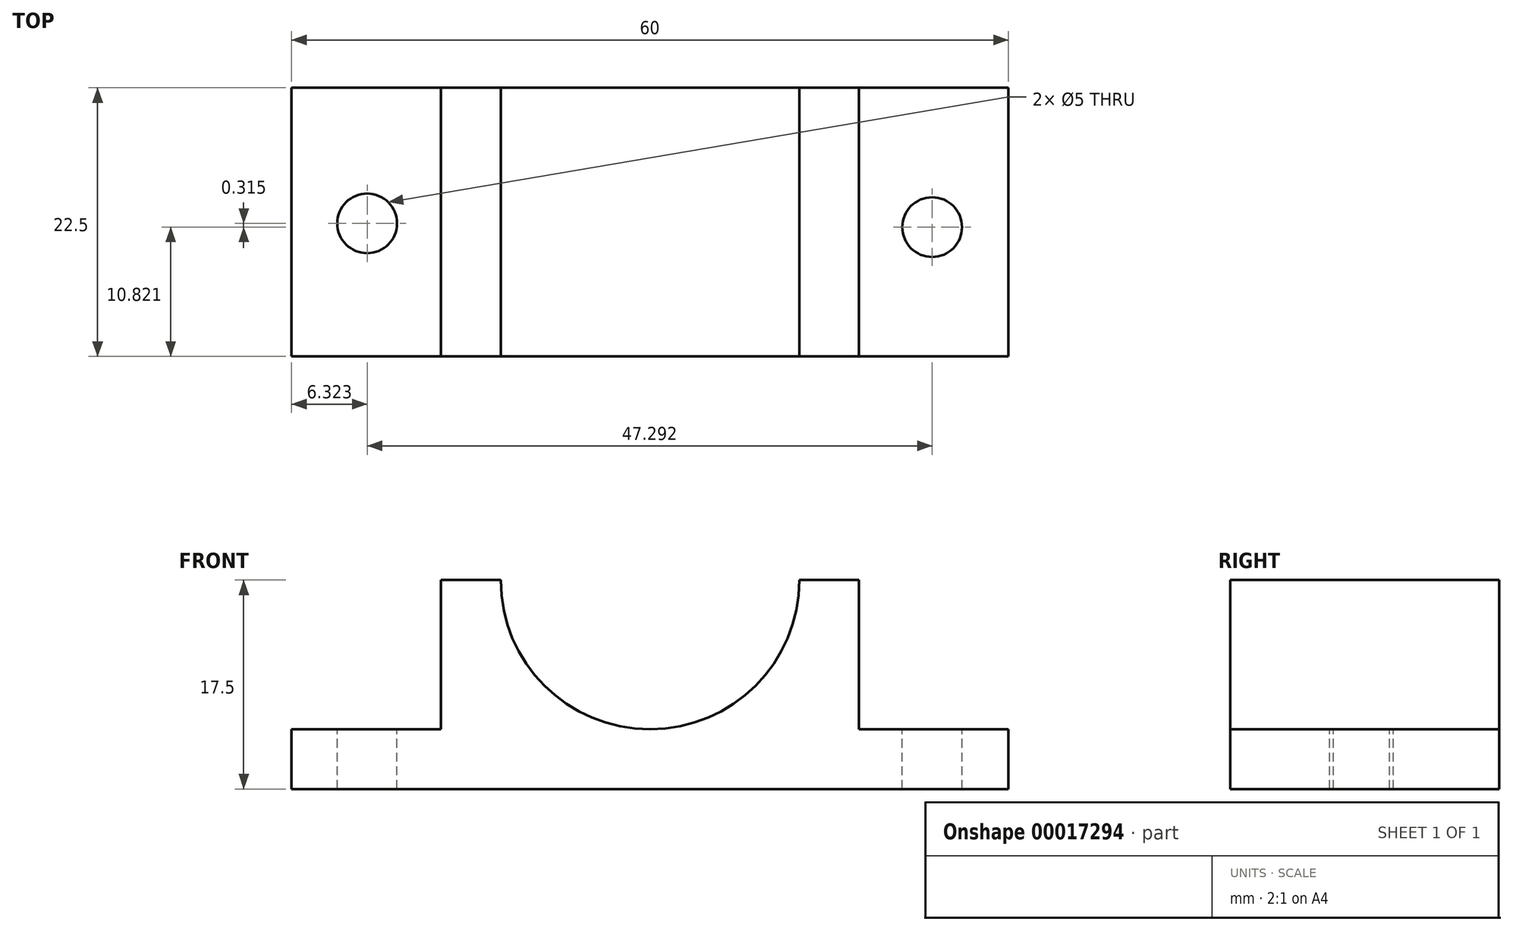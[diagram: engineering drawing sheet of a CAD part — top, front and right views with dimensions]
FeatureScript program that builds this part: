
annotation { "Feature Type Name" : "Feature", "Feature Type Description" : "" }
export const myFeature = defineFeature(function(context is Context, id is Id, definition is map)
    precondition{}
    {
        {
            var Q0;
            Q0=qCreatedBy(makeId("Front.planeOp"),FACE);
            var sketch = newSketch(context, id + "F0", { "sketchPlane" : qUnion([Q0])});
            skLineSegment(sketch, "E0", {"start": v(0, 0) * mm, "end": v(0, 5) * mm});
            skLineSegment(sketch, "E1", {"start": v(0, 5) * mm, "end": v(-12.5, 5) * mm});
            skLineSegment(sketch, "E2", {"start": v(-12.5, 5) * mm, "end": v(-12.5, 17.5) * mm});
            skLineSegment(sketch, "E3", {"start": v(-12.5, 17.5) * mm, "end": v(-17.5, 17.5) * mm});
            skLineSegment(sketch, "E4", {"start": v(-17.5, 17.5) * mm, "end": v(-42.5, 17.5) * mm});
            skLineSegment(sketch, "E5", {"start": v(-42.5, 17.5) * mm, "end": v(-47.5, 17.5) * mm});
            skLineSegment(sketch, "E6", {"start": v(-47.5, 17.5) * mm, "end": v(-47.5, 5) * mm});
            skLineSegment(sketch, "E7", {"start": v(-47.5, 5) * mm, "end": v(-60, 5) * mm});
            skLineSegment(sketch, "E8", {"start": v(-60, 5) * mm, "end": v(-60, 0) * mm});
            skLineSegment(sketch, "E9", {"start": v(-60, 0) * mm, "end": v(0, 0) * mm});
            skArc(sketch, "E10", {"start": v(-42.5, 17.5) * mm, "mid": v(-30, 5) * mm, "end": v(-17.5, 17.5) * mm});
            skSolve(sketch);
        }
        {
            var Q0;
            Q0=makeQuery(id+"F0.imprint","IMPRINT",FACE,{"disambiguationData":[TD([[makeQuery(id+"F0.imprint","IMPRINT",EDGE,{"derivedFrom":sQuery(id+"F0.wireOp",EDGE,"E0")}),1.0]])]});
            extrude(context, id + "F1", {"entities" : qUnion([Q0]), "depth" : 22.5 * mm});
        }
        {
            var Q0;
            Q0=makeQuery(id+"F1.opExtrude","SWEPT_FACE",FACE,{"disambiguationData":[OSD([sQuery(id+"F0.wireOp",EDGE,"E1")])]});
            var sketch = newSketch(context, id + "F2", { "sketchPlane" : qUnion([Q0])});
            skCircle(sketch, "E11", {"center": v(-6.38, -11.68) * mm, "radius": 2.5 * mm});
            skSolve(sketch);
        }
        {
            var Q0;
            Q0=makeQuery(id+"F2.imprint","IMPRINT",FACE,{"disambiguationData":[TD([[makeQuery(id+"F2.imprint","IMPRINT",EDGE,{"derivedFrom":sQuery(id+"F2.wireOp",EDGE,"E11")}),1.0]])]});
            extrude(context, id + "F3", {"entities" : qUnion([Q0]), "operationType" : NewBodyOperationType.REMOVE, "oppositeDirection" : true, "depth" : 25 * mm});
        }
        {
            var Q0;
            Q0=makeQuery(id+"F1.opExtrude","SWEPT_FACE",FACE,{"disambiguationData":[OSD([sQuery(id+"F0.wireOp",EDGE,"E7")])]});
            var sketch = newSketch(context, id + "F4", { "sketchPlane" : qUnion([Q0])});
            skCircle(sketch, "E12", {"center": v(-53.68, -11.36) * mm, "radius": 2.5 * mm});
            skSolve(sketch);
        }
        {
            var Q0;
            Q0=makeQuery(id+"F4.imprint","IMPRINT",FACE,{"disambiguationData":[TD([[makeQuery(id+"F4.imprint","IMPRINT",EDGE,{"derivedFrom":sQuery(id+"F4.wireOp",EDGE,"E12")}),1.0]])]});
            extrude(context, id + "F5", {"entities" : qUnion([Q0]), "operationType" : NewBodyOperationType.REMOVE, "oppositeDirection" : true, "depth" : 25 * mm});
        }
    });
